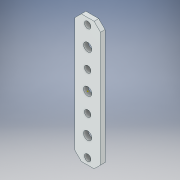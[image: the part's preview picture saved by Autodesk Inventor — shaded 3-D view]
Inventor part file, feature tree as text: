
AUTODESK INVENTOR PART (.ipt)
format: ipt  version: 2017 (Build 210142000, 142)  size: 111,616 bytes
history: native  units: in
note: dims shown in document units (in); Inventor stores cm internally (conversion verified against a paired STEP export)
features: sketch x1, other x1
ambient origin geometry x8: Origin, YZ Plane, XZ Plane, XY Plane, X Axis, Y Axis, Z Axis, Center Point
bodies: Solid1 (feature_tree)
feature tree (2):
  sketch  "Sketch1"
  other  "Break-Corner1"
